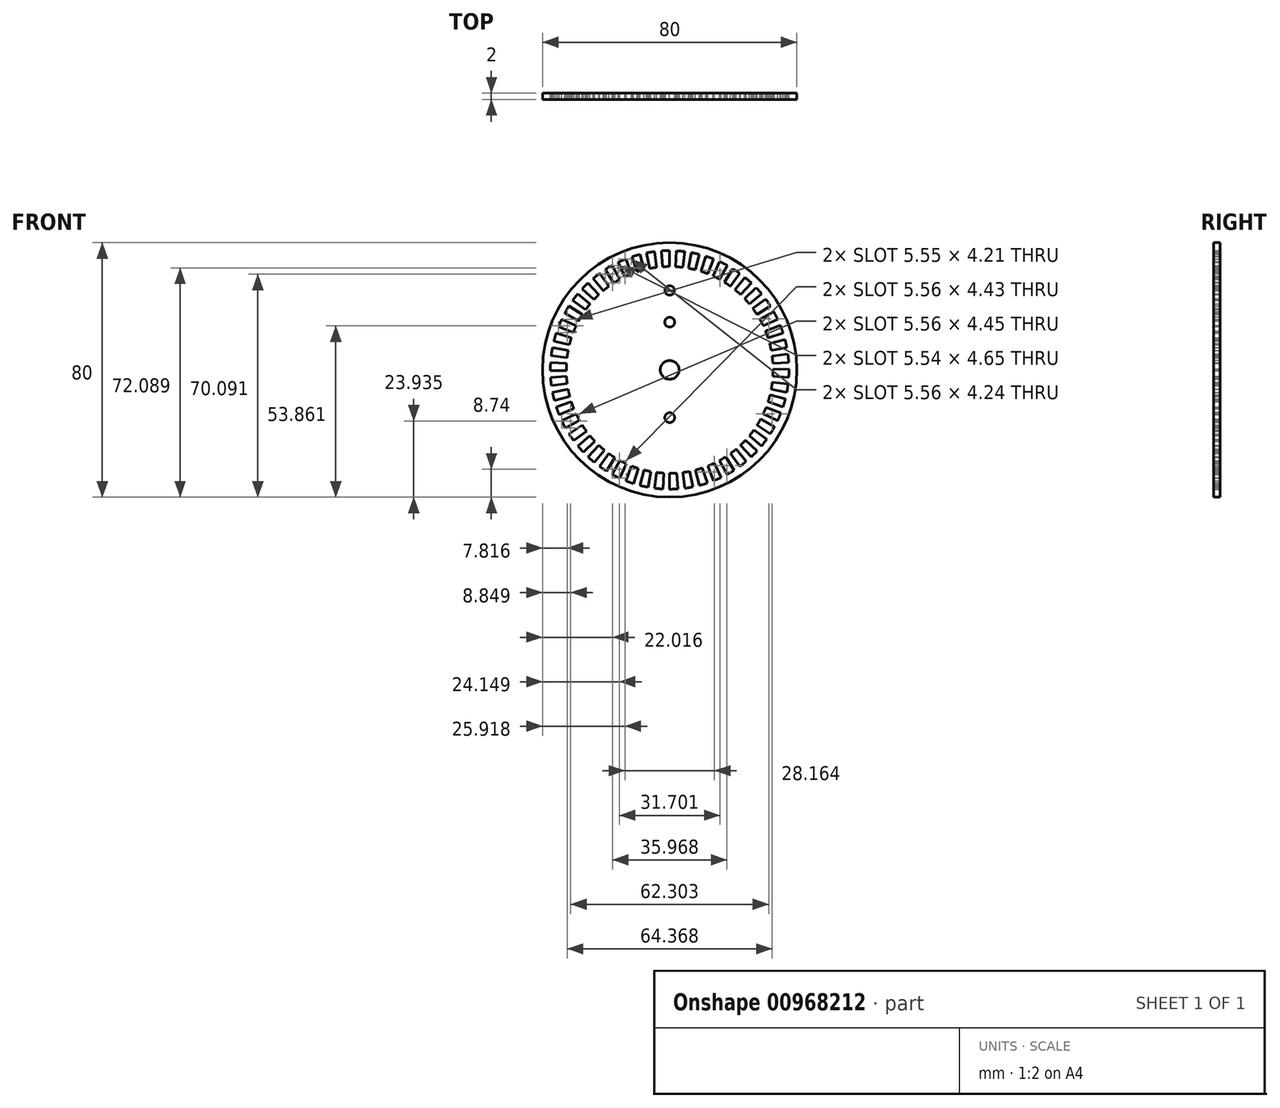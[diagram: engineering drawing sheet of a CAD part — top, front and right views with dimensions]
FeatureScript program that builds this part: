
annotation { "Feature Type Name" : "Feature", "Feature Type Description" : "" }
export const myFeature = defineFeature(function(context is Context, id is Id, definition is map)
    precondition{}
    {
        {
            var Q0;
            Q0=qCreatedBy(makeId("Front.planeOp"),FACE);
            var sketch = newSketch(context, id + "F0", { "sketchPlane" : qUnion([Q0])});
            skCircle(sketch, "E0", {"center": v(0, 0) * mm, "radius": 40 * mm});
            skSolve(sketch);
        }
        {
            var Q0;
            Q0=qSketchRegion(id+"F0",true);
            extrude(context, id + "F1", {"entities" : qUnion([Q0]), "endBound" : BoundingType.SYMMETRIC, "depth" : 2 * mm, "offsetDistance" : 25 * mm});
        }
        {
            var Q0;
            Q0=qCreatedBy(makeId("Front.planeOp"),FACE);
            var sketch = newSketch(context, id + "F2", { "sketchPlane" : qUnion([Q0])});
            skCircle(sketch, "E1", {"center": v(0, 0) * mm, "radius": 2.95 * mm});
            skCircle(sketch, "E2", {"center": v(0, 25) * mm, "radius": 1.5 * mm});
            skCircle(sketch, "E3", {"center": v(0, 15) * mm, "radius": 1.55 * mm});
            skCircle(sketch, "E4", {"center": v(0, -15) * mm, "radius": 1.55 * mm});
            skSolve(sketch);
        }
        {
            var Q0;
            Q0=qSketchRegion(id+"F2",true);
            extrude(context, id + "F3", {"entities" : qUnion([Q0]), "operationType" : NewBodyOperationType.REMOVE, "endBound" : BoundingType.SYMMETRIC, "oppositeDirection" : true, "depth" : 12 * mm, "offsetDistance" : 25 * mm});
        }
        {
            var Q0;
            Q0=qCreatedBy(makeId("Front.planeOp"),FACE);
            var sketch = newSketch(context, id + "F4", { "sketchPlane" : qUnion([Q0])});
            skLineSegment(sketch, "E5", {"start": v(0, 32.5) * mm, "end": v(0, 37.5) * mm});
            skArc(sketch, "E6", {"start": v(0, 37.5) * mm, "mid": v(-1.3, 37.48) * mm, "end": v(-2.61, 37.4) * mm});
            skArc(sketch, "E7", {"start": v(0, 32.5) * mm, "mid": v(-1.13, 32.48) * mm, "end": v(-2.26, 32.42) * mm});
            skLineSegment(sketch, "E8", {"start": v(-2.26, 32.42) * mm, "end": v(-2.61, 37.4) * mm});
            skLineSegment(sketch, "E9.1.0", {"start": v(-6.3, 31.88) * mm, "end": v(-7.28, 36.79) * mm});
            skLineSegment(sketch, "E9.1.1", {"start": v(-4.07, 32.24) * mm, "end": v(-4.7, 37.2) * mm});
            skArc(sketch, "E9.1.2", {"start": v(-4.7, 37.2) * mm, "mid": v(-6, 37.02) * mm, "end": v(-7.28, 36.79) * mm});
            skArc(sketch, "E9.1.3", {"start": v(-4.07, 32.24) * mm, "mid": v(-5.2, 32.08) * mm, "end": v(-6.3, 31.88) * mm});
            skLineSegment(sketch, "E9.2.0", {"start": v(-10.26, 30.84) * mm, "end": v(-11.83, 35.58) * mm});
            skLineSegment(sketch, "E9.2.1", {"start": v(-8.08, 31.48) * mm, "end": v(-9.33, 36.32) * mm});
            skArc(sketch, "E9.2.2", {"start": v(-9.33, 36.32) * mm, "mid": v(-10.59, 35.97) * mm, "end": v(-11.83, 35.58) * mm});
            skArc(sketch, "E9.2.3", {"start": v(-8.08, 31.48) * mm, "mid": v(-9.17, 31.18) * mm, "end": v(-10.26, 30.84) * mm});
            skLineSegment(sketch, "E9.3.0", {"start": v(-14.04, 29.31) * mm, "end": v(-16.2, 33.82) * mm});
            skLineSegment(sketch, "E9.3.1", {"start": v(-11.96, 30.22) * mm, "end": v(-13.8, 34.87) * mm});
            skArc(sketch, "E9.3.2", {"start": v(-13.8, 34.87) * mm, "mid": v(-15.01, 34.36) * mm, "end": v(-16.2, 33.82) * mm});
            skArc(sketch, "E9.3.3", {"start": v(-11.96, 30.22) * mm, "mid": v(-13, 29.78) * mm, "end": v(-14.04, 29.31) * mm});
            skLineSegment(sketch, "E9.4.0", {"start": v(-17.6, 27.32) * mm, "end": v(-20.31, 31.52) * mm});
            skLineSegment(sketch, "E9.4.1", {"start": v(-15.66, 28.48) * mm, "end": v(-18.07, 32.86) * mm});
            skArc(sketch, "E9.4.2", {"start": v(-18.07, 32.86) * mm, "mid": v(-19.2, 32.21) * mm, "end": v(-20.31, 31.52) * mm});
            skArc(sketch, "E9.4.3", {"start": v(-15.66, 28.48) * mm, "mid": v(-16.64, 27.92) * mm, "end": v(-17.6, 27.32) * mm});
            skLineSegment(sketch, "E9.5.0", {"start": v(-20.89, 24.9) * mm, "end": v(-24.1, 28.73) * mm});
            skLineSegment(sketch, "E9.5.1", {"start": v(-19.1, 26.3) * mm, "end": v(-22.04, 30.34) * mm});
            skArc(sketch, "E9.5.2", {"start": v(-22.04, 30.34) * mm, "mid": v(-23.09, 29.55) * mm, "end": v(-24.1, 28.73) * mm});
            skArc(sketch, "E9.5.3", {"start": v(-19.1, 26.3) * mm, "mid": v(-20, 25.61) * mm, "end": v(-20.89, 24.9) * mm});
            skLineSegment(sketch, "E9.6.0", {"start": v(-23.84, 22.08) * mm, "end": v(-27.51, 25.48) * mm});
            skLineSegment(sketch, "E9.6.1", {"start": v(-22.25, 23.7) * mm, "end": v(-25.67, 27.34) * mm});
            skArc(sketch, "E9.6.2", {"start": v(-25.67, 27.34) * mm, "mid": v(-26.6, 26.43) * mm, "end": v(-27.51, 25.48) * mm});
            skArc(sketch, "E9.6.3", {"start": v(-22.25, 23.7) * mm, "mid": v(-23.06, 22.9) * mm, "end": v(-23.84, 22.08) * mm});
            skLineSegment(sketch, "E9.7.0", {"start": v(-26.42, 18.92) * mm, "end": v(-30.49, 21.83) * mm});
            skLineSegment(sketch, "E9.7.1", {"start": v(-25.04, 20.72) * mm, "end": v(-28.9, 23.9) * mm});
            skArc(sketch, "E9.7.2", {"start": v(-28.9, 23.9) * mm, "mid": v(-29.7, 22.88) * mm, "end": v(-30.49, 21.83) * mm});
            skArc(sketch, "E9.7.3", {"start": v(-25.04, 20.72) * mm, "mid": v(-25.75, 19.83) * mm, "end": v(-26.42, 18.92) * mm});
            skLineSegment(sketch, "E9.8.0", {"start": v(-28.59, 15.46) * mm, "end": v(-32.98, 17.84) * mm});
            skLineSegment(sketch, "E9.8.1", {"start": v(-27.44, 17.41) * mm, "end": v(-31.66, 20.1) * mm});
            skArc(sketch, "E9.8.2", {"start": v(-31.66, 20.1) * mm, "mid": v(-32.34, 18.98) * mm, "end": v(-32.98, 17.84) * mm});
            skArc(sketch, "E9.8.3", {"start": v(-27.44, 17.41) * mm, "mid": v(-28.03, 16.45) * mm, "end": v(-28.59, 15.46) * mm});
            skLineSegment(sketch, "E9.9.0", {"start": v(-30.3, 11.76) * mm, "end": v(-34.96, 13.56) * mm});
            skLineSegment(sketch, "E9.9.1", {"start": v(-29.4, 13.84) * mm, "end": v(-33.93, 15.97) * mm});
            skArc(sketch, "E9.9.2", {"start": v(-33.93, 15.97) * mm, "mid": v(-34.47, 14.77) * mm, "end": v(-34.96, 13.56) * mm});
            skArc(sketch, "E9.9.3", {"start": v(-29.4, 13.84) * mm, "mid": v(-29.87, 12.8) * mm, "end": v(-30.3, 11.76) * mm});
            skLineSegment(sketch, "E9.10.0", {"start": v(-31.53, 7.87) * mm, "end": v(-36.39, 9.08) * mm});
            skLineSegment(sketch, "E9.10.1", {"start": v(-30.9, 10.04) * mm, "end": v(-35.66, 11.59) * mm});
            skArc(sketch, "E9.10.2", {"start": v(-35.66, 11.59) * mm, "mid": v(-36.05, 10.34) * mm, "end": v(-36.39, 9.08) * mm});
            skArc(sketch, "E9.10.3", {"start": v(-30.9, 10.04) * mm, "mid": v(-31.24, 8.96) * mm, "end": v(-31.53, 7.87) * mm});
            skLineSegment(sketch, "E9.11.0", {"start": v(-32.27, 3.85) * mm, "end": v(-37.24, 4.44) * mm});
            skLineSegment(sketch, "E9.11.1", {"start": v(-31.92, 6.09) * mm, "end": v(-36.84, 7.03) * mm});
            skArc(sketch, "E9.11.2", {"start": v(-36.84, 7.03) * mm, "mid": v(-37.06, 5.74) * mm, "end": v(-37.24, 4.44) * mm});
            skArc(sketch, "E9.11.3", {"start": v(-31.92, 6.09) * mm, "mid": v(-32.12, 4.97) * mm, "end": v(-32.27, 3.85) * mm});
            skLineSegment(sketch, "E9.12.0", {"start": v(-32.5, -0.22) * mm, "end": v(-37.5, -0.26) * mm});
            skLineSegment(sketch, "E9.12.1", {"start": v(-32.44, 2.04) * mm, "end": v(-37.43, 2.35) * mm});
            skArc(sketch, "E9.12.2", {"start": v(-37.43, 2.35) * mm, "mid": v(-37.49, 1.05) * mm, "end": v(-37.5, -0.26) * mm});
            skArc(sketch, "E9.12.3", {"start": v(-32.44, 2.04) * mm, "mid": v(-32.49, 0.9) * mm, "end": v(-32.5, -0.22) * mm});
            skLineSegment(sketch, "E9.13.0", {"start": v(-32.21, -4.3) * mm, "end": v(-37.17, -4.96) * mm});
            skLineSegment(sketch, "E9.13.1", {"start": v(-32.44, -2.04) * mm, "end": v(-37.43, -2.35) * mm});
            skArc(sketch, "E9.13.2", {"start": v(-37.43, -2.35) * mm, "mid": v(-37.32, -3.66) * mm, "end": v(-37.17, -4.96) * mm});
            skArc(sketch, "E9.13.3", {"start": v(-32.44, -2.04) * mm, "mid": v(-32.35, -3.17) * mm, "end": v(-32.21, -4.3) * mm});
            skLineSegment(sketch, "E9.14.0", {"start": v(-31.42, -8.3) * mm, "end": v(-36.26, -9.58) * mm});
            skLineSegment(sketch, "E9.14.1", {"start": v(-31.92, -6.09) * mm, "end": v(-36.84, -7.03) * mm});
            skArc(sketch, "E9.14.2", {"start": v(-36.84, -7.03) * mm, "mid": v(-36.57, -8.3) * mm, "end": v(-36.26, -9.58) * mm});
            skArc(sketch, "E9.14.3", {"start": v(-31.92, -6.09) * mm, "mid": v(-31.7, -7.2) * mm, "end": v(-31.42, -8.3) * mm});
            skLineSegment(sketch, "E9.15.0", {"start": v(-30.13, -12.17) * mm, "end": v(-34.77, -14.04) * mm});
            skLineSegment(sketch, "E9.15.1", {"start": v(-30.9, -10.04) * mm, "end": v(-35.66, -11.59) * mm});
            skArc(sketch, "E9.15.2", {"start": v(-35.66, -11.59) * mm, "mid": v(-35.24, -12.82) * mm, "end": v(-34.77, -14.04) * mm});
            skArc(sketch, "E9.15.3", {"start": v(-30.9, -10.04) * mm, "mid": v(-30.54, -11.11) * mm, "end": v(-30.13, -12.17) * mm});
            skLineSegment(sketch, "E9.16.0", {"start": v(-28.37, -15.85) * mm, "end": v(-32.74, -18.3) * mm});
            skLineSegment(sketch, "E9.16.1", {"start": v(-29.4, -13.84) * mm, "end": v(-33.93, -15.97) * mm});
            skArc(sketch, "E9.16.2", {"start": v(-33.93, -15.97) * mm, "mid": v(-33.35, -17.14) * mm, "end": v(-32.74, -18.3) * mm});
            skArc(sketch, "E9.16.3", {"start": v(-29.4, -13.84) * mm, "mid": v(-28.9, -14.85) * mm, "end": v(-28.37, -15.85) * mm});
            skLineSegment(sketch, "E9.17.0", {"start": v(-26.16, -19.28) * mm, "end": v(-30.19, -22.25) * mm});
            skLineSegment(sketch, "E9.17.1", {"start": v(-27.44, -17.41) * mm, "end": v(-31.66, -20.1) * mm});
            skArc(sketch, "E9.17.2", {"start": v(-31.66, -20.1) * mm, "mid": v(-30.94, -21.18) * mm, "end": v(-30.19, -22.25) * mm});
            skArc(sketch, "E9.17.3", {"start": v(-27.44, -17.41) * mm, "mid": v(-26.82, -18.36) * mm, "end": v(-26.16, -19.28) * mm});
            skLineSegment(sketch, "E9.18.0", {"start": v(-23.54, -22.41) * mm, "end": v(-27.16, -25.86) * mm});
            skLineSegment(sketch, "E9.18.1", {"start": v(-25.04, -20.72) * mm, "end": v(-28.9, -23.9) * mm});
            skArc(sketch, "E9.18.2", {"start": v(-28.9, -23.9) * mm, "mid": v(-28.04, -24.9) * mm, "end": v(-27.16, -25.86) * mm});
            skArc(sketch, "E9.18.3", {"start": v(-25.04, -20.72) * mm, "mid": v(-24.3, -21.58) * mm, "end": v(-23.54, -22.41) * mm});
            skLineSegment(sketch, "E9.19.0", {"start": v(-20.54, -25.18) * mm, "end": v(-23.7, -29.06) * mm});
            skLineSegment(sketch, "E9.19.1", {"start": v(-22.25, -23.7) * mm, "end": v(-25.67, -27.34) * mm});
            skArc(sketch, "E9.19.2", {"start": v(-25.67, -27.34) * mm, "mid": v(-24.7, -28.21) * mm, "end": v(-23.7, -29.06) * mm});
            skArc(sketch, "E9.19.3", {"start": v(-22.25, -23.7) * mm, "mid": v(-21.4, -24.45) * mm, "end": v(-20.54, -25.18) * mm});
            skLineSegment(sketch, "E9.20.0", {"start": v(-17.23, -27.56) * mm, "end": v(-19.88, -31.8) * mm});
            skLineSegment(sketch, "E9.20.1", {"start": v(-19.1, -26.3) * mm, "end": v(-22.04, -30.34) * mm});
            skArc(sketch, "E9.20.2", {"start": v(-22.04, -30.34) * mm, "mid": v(-20.97, -31.09) * mm, "end": v(-19.88, -31.8) * mm});
            skArc(sketch, "E9.20.3", {"start": v(-19.1, -26.3) * mm, "mid": v(-18.18, -26.94) * mm, "end": v(-17.23, -27.56) * mm});
            skLineSegment(sketch, "E9.21.0", {"start": v(-13.64, -29.5) * mm, "end": v(-15.73, -34.04) * mm});
            skLineSegment(sketch, "E9.21.1", {"start": v(-15.66, -28.48) * mm, "end": v(-18.07, -32.86) * mm});
            skArc(sketch, "E9.21.2", {"start": v(-18.07, -32.86) * mm, "mid": v(-16.9, -33.47) * mm, "end": v(-15.73, -34.04) * mm});
            skArc(sketch, "E9.21.3", {"start": v(-15.66, -28.48) * mm, "mid": v(-14.66, -29) * mm, "end": v(-13.64, -29.5) * mm});
            skLineSegment(sketch, "E9.22.0", {"start": v(-9.83, -30.98) * mm, "end": v(-11.34, -35.74) * mm});
            skLineSegment(sketch, "E9.22.1", {"start": v(-11.96, -30.22) * mm, "end": v(-13.8, -34.87) * mm});
            skArc(sketch, "E9.22.2", {"start": v(-13.8, -34.87) * mm, "mid": v(-12.58, -35.33) * mm, "end": v(-11.34, -35.74) * mm});
            skArc(sketch, "E9.22.3", {"start": v(-11.96, -30.22) * mm, "mid": v(-10.9, -30.62) * mm, "end": v(-9.83, -30.98) * mm});
            skLineSegment(sketch, "E9.23.0", {"start": v(-5.87, -31.97) * mm, "end": v(-6.77, -36.88) * mm});
            skLineSegment(sketch, "E9.23.1", {"start": v(-8.08, -31.48) * mm, "end": v(-9.33, -36.32) * mm});
            skArc(sketch, "E9.23.2", {"start": v(-9.33, -36.32) * mm, "mid": v(-8.05, -36.62) * mm, "end": v(-6.77, -36.88) * mm});
            skArc(sketch, "E9.23.3", {"start": v(-8.08, -31.48) * mm, "mid": v(-6.98, -31.74) * mm, "end": v(-5.87, -31.97) * mm});
            skLineSegment(sketch, "E9.24.0", {"start": v(-1.82, -32.45) * mm, "end": v(-2.1, -37.44) * mm});
            skLineSegment(sketch, "E9.24.1", {"start": v(-4.07, -32.24) * mm, "end": v(-4.7, -37.2) * mm});
            skArc(sketch, "E9.24.2", {"start": v(-4.7, -37.2) * mm, "mid": v(-3.4, -37.35) * mm, "end": v(-2.1, -37.44) * mm});
            skArc(sketch, "E9.24.3", {"start": v(-4.07, -32.24) * mm, "mid": v(-2.95, -32.37) * mm, "end": v(-1.82, -32.45) * mm});
            skLineSegment(sketch, "E9.25.0", {"start": v(2.26, -32.42) * mm, "end": v(2.61, -37.4) * mm});
            skLineSegment(sketch, "E9.25.1", {"start": v(0, -32.5) * mm, "end": v(0, -37.5) * mm});
            skArc(sketch, "E9.25.2", {"start": v(0, -37.5) * mm, "mid": v(1.3, -37.48) * mm, "end": v(2.61, -37.4) * mm});
            skArc(sketch, "E9.25.3", {"start": v(0, -32.5) * mm, "mid": v(1.13, -32.48) * mm, "end": v(2.26, -32.42) * mm});
            skLineSegment(sketch, "E9.26.0", {"start": v(6.3, -31.88) * mm, "end": v(7.28, -36.79) * mm});
            skLineSegment(sketch, "E9.26.1", {"start": v(4.07, -32.24) * mm, "end": v(4.7, -37.2) * mm});
            skArc(sketch, "E9.26.2", {"start": v(4.7, -37.2) * mm, "mid": v(6, -37.02) * mm, "end": v(7.28, -36.79) * mm});
            skArc(sketch, "E9.26.3", {"start": v(4.07, -32.24) * mm, "mid": v(5.2, -32.08) * mm, "end": v(6.3, -31.88) * mm});
            skLineSegment(sketch, "E9.27.0", {"start": v(10.26, -30.84) * mm, "end": v(11.83, -35.58) * mm});
            skLineSegment(sketch, "E9.27.1", {"start": v(8.08, -31.48) * mm, "end": v(9.33, -36.32) * mm});
            skArc(sketch, "E9.27.2", {"start": v(9.33, -36.32) * mm, "mid": v(10.59, -35.97) * mm, "end": v(11.83, -35.58) * mm});
            skArc(sketch, "E9.27.3", {"start": v(8.08, -31.48) * mm, "mid": v(9.17, -31.18) * mm, "end": v(10.26, -30.84) * mm});
            skLineSegment(sketch, "E9.28.0", {"start": v(14.04, -29.31) * mm, "end": v(16.2, -33.82) * mm});
            skLineSegment(sketch, "E9.28.1", {"start": v(11.96, -30.22) * mm, "end": v(13.8, -34.87) * mm});
            skArc(sketch, "E9.28.2", {"start": v(13.8, -34.87) * mm, "mid": v(15.01, -34.36) * mm, "end": v(16.2, -33.82) * mm});
            skArc(sketch, "E9.28.3", {"start": v(11.96, -30.22) * mm, "mid": v(13, -29.78) * mm, "end": v(14.04, -29.31) * mm});
            skLineSegment(sketch, "E9.29.0", {"start": v(17.6, -27.32) * mm, "end": v(20.31, -31.52) * mm});
            skLineSegment(sketch, "E9.29.1", {"start": v(15.66, -28.48) * mm, "end": v(18.07, -32.86) * mm});
            skArc(sketch, "E9.29.2", {"start": v(18.07, -32.86) * mm, "mid": v(19.2, -32.21) * mm, "end": v(20.31, -31.52) * mm});
            skArc(sketch, "E9.29.3", {"start": v(15.66, -28.48) * mm, "mid": v(16.64, -27.92) * mm, "end": v(17.6, -27.32) * mm});
            skLineSegment(sketch, "E9.30.0", {"start": v(20.89, -24.9) * mm, "end": v(24.1, -28.73) * mm});
            skLineSegment(sketch, "E9.30.1", {"start": v(19.1, -26.3) * mm, "end": v(22.04, -30.34) * mm});
            skArc(sketch, "E9.30.2", {"start": v(22.04, -30.34) * mm, "mid": v(23.09, -29.55) * mm, "end": v(24.1, -28.73) * mm});
            skArc(sketch, "E9.30.3", {"start": v(19.1, -26.3) * mm, "mid": v(20, -25.61) * mm, "end": v(20.89, -24.9) * mm});
            skLineSegment(sketch, "E9.31.0", {"start": v(23.84, -22.08) * mm, "end": v(27.51, -25.48) * mm});
            skLineSegment(sketch, "E9.31.1", {"start": v(22.25, -23.7) * mm, "end": v(25.67, -27.34) * mm});
            skArc(sketch, "E9.31.2", {"start": v(25.67, -27.34) * mm, "mid": v(26.6, -26.43) * mm, "end": v(27.51, -25.48) * mm});
            skArc(sketch, "E9.31.3", {"start": v(22.25, -23.7) * mm, "mid": v(23.06, -22.9) * mm, "end": v(23.84, -22.08) * mm});
            skLineSegment(sketch, "E9.32.0", {"start": v(26.42, -18.92) * mm, "end": v(30.49, -21.83) * mm});
            skLineSegment(sketch, "E9.32.1", {"start": v(25.04, -20.72) * mm, "end": v(28.9, -23.9) * mm});
            skArc(sketch, "E9.32.2", {"start": v(28.9, -23.9) * mm, "mid": v(29.7, -22.88) * mm, "end": v(30.49, -21.83) * mm});
            skArc(sketch, "E9.32.3", {"start": v(25.04, -20.72) * mm, "mid": v(25.75, -19.83) * mm, "end": v(26.42, -18.92) * mm});
            skLineSegment(sketch, "E9.33.0", {"start": v(28.59, -15.46) * mm, "end": v(32.98, -17.84) * mm});
            skLineSegment(sketch, "E9.33.1", {"start": v(27.44, -17.41) * mm, "end": v(31.66, -20.1) * mm});
            skArc(sketch, "E9.33.2", {"start": v(31.66, -20.1) * mm, "mid": v(32.34, -18.98) * mm, "end": v(32.98, -17.84) * mm});
            skArc(sketch, "E9.33.3", {"start": v(27.44, -17.41) * mm, "mid": v(28.03, -16.45) * mm, "end": v(28.59, -15.46) * mm});
            skLineSegment(sketch, "E9.34.0", {"start": v(30.3, -11.76) * mm, "end": v(34.96, -13.56) * mm});
            skLineSegment(sketch, "E9.34.1", {"start": v(29.4, -13.84) * mm, "end": v(33.93, -15.97) * mm});
            skArc(sketch, "E9.34.2", {"start": v(33.93, -15.97) * mm, "mid": v(34.47, -14.77) * mm, "end": v(34.96, -13.56) * mm});
            skArc(sketch, "E9.34.3", {"start": v(29.4, -13.84) * mm, "mid": v(29.87, -12.8) * mm, "end": v(30.3, -11.76) * mm});
            skLineSegment(sketch, "E9.35.0", {"start": v(31.53, -7.87) * mm, "end": v(36.39, -9.08) * mm});
            skLineSegment(sketch, "E9.35.1", {"start": v(30.9, -10.04) * mm, "end": v(35.66, -11.59) * mm});
            skArc(sketch, "E9.35.2", {"start": v(35.66, -11.59) * mm, "mid": v(36.05, -10.34) * mm, "end": v(36.39, -9.08) * mm});
            skArc(sketch, "E9.35.3", {"start": v(30.9, -10.04) * mm, "mid": v(31.24, -8.96) * mm, "end": v(31.53, -7.87) * mm});
            skLineSegment(sketch, "E9.36.0", {"start": v(32.27, -3.85) * mm, "end": v(37.24, -4.44) * mm});
            skLineSegment(sketch, "E9.36.1", {"start": v(31.92, -6.09) * mm, "end": v(36.84, -7.03) * mm});
            skArc(sketch, "E9.36.2", {"start": v(36.84, -7.03) * mm, "mid": v(37.06, -5.74) * mm, "end": v(37.24, -4.44) * mm});
            skArc(sketch, "E9.36.3", {"start": v(31.92, -6.09) * mm, "mid": v(32.12, -4.97) * mm, "end": v(32.27, -3.85) * mm});
            skLineSegment(sketch, "E9.37.0", {"start": v(32.5, 0.22) * mm, "end": v(37.5, 0.26) * mm});
            skLineSegment(sketch, "E9.37.1", {"start": v(32.44, -2.04) * mm, "end": v(37.43, -2.35) * mm});
            skArc(sketch, "E9.37.2", {"start": v(37.43, -2.35) * mm, "mid": v(37.49, -1.05) * mm, "end": v(37.5, 0.26) * mm});
            skArc(sketch, "E9.37.3", {"start": v(32.44, -2.04) * mm, "mid": v(32.49, -0.9) * mm, "end": v(32.5, 0.22) * mm});
            skLineSegment(sketch, "E9.38.0", {"start": v(32.21, 4.3) * mm, "end": v(37.17, 4.96) * mm});
            skLineSegment(sketch, "E9.38.1", {"start": v(32.44, 2.04) * mm, "end": v(37.43, 2.35) * mm});
            skArc(sketch, "E9.38.2", {"start": v(37.43, 2.35) * mm, "mid": v(37.32, 3.66) * mm, "end": v(37.17, 4.96) * mm});
            skArc(sketch, "E9.38.3", {"start": v(32.44, 2.04) * mm, "mid": v(32.35, 3.17) * mm, "end": v(32.21, 4.3) * mm});
            skLineSegment(sketch, "E9.39.0", {"start": v(31.42, 8.3) * mm, "end": v(36.26, 9.58) * mm});
            skLineSegment(sketch, "E9.39.1", {"start": v(31.92, 6.09) * mm, "end": v(36.84, 7.03) * mm});
            skArc(sketch, "E9.39.2", {"start": v(36.84, 7.03) * mm, "mid": v(36.57, 8.3) * mm, "end": v(36.26, 9.58) * mm});
            skArc(sketch, "E9.39.3", {"start": v(31.92, 6.09) * mm, "mid": v(31.7, 7.2) * mm, "end": v(31.42, 8.3) * mm});
            skLineSegment(sketch, "E9.40.0", {"start": v(30.13, 12.17) * mm, "end": v(34.77, 14.04) * mm});
            skLineSegment(sketch, "E9.40.1", {"start": v(30.9, 10.04) * mm, "end": v(35.66, 11.59) * mm});
            skArc(sketch, "E9.40.2", {"start": v(35.66, 11.59) * mm, "mid": v(35.24, 12.82) * mm, "end": v(34.77, 14.04) * mm});
            skArc(sketch, "E9.40.3", {"start": v(30.9, 10.04) * mm, "mid": v(30.54, 11.11) * mm, "end": v(30.13, 12.17) * mm});
            skLineSegment(sketch, "E9.41.0", {"start": v(28.37, 15.85) * mm, "end": v(32.74, 18.3) * mm});
            skLineSegment(sketch, "E9.41.1", {"start": v(29.4, 13.84) * mm, "end": v(33.93, 15.97) * mm});
            skArc(sketch, "E9.41.2", {"start": v(33.93, 15.97) * mm, "mid": v(33.35, 17.14) * mm, "end": v(32.74, 18.3) * mm});
            skArc(sketch, "E9.41.3", {"start": v(29.4, 13.84) * mm, "mid": v(28.9, 14.85) * mm, "end": v(28.37, 15.85) * mm});
            skLineSegment(sketch, "E9.42.0", {"start": v(26.16, 19.28) * mm, "end": v(30.19, 22.25) * mm});
            skLineSegment(sketch, "E9.42.1", {"start": v(27.44, 17.41) * mm, "end": v(31.66, 20.1) * mm});
            skArc(sketch, "E9.42.2", {"start": v(31.66, 20.1) * mm, "mid": v(30.94, 21.18) * mm, "end": v(30.19, 22.25) * mm});
            skArc(sketch, "E9.42.3", {"start": v(27.44, 17.41) * mm, "mid": v(26.82, 18.36) * mm, "end": v(26.16, 19.28) * mm});
            skLineSegment(sketch, "E9.43.0", {"start": v(23.54, 22.41) * mm, "end": v(27.16, 25.86) * mm});
            skLineSegment(sketch, "E9.43.1", {"start": v(25.04, 20.72) * mm, "end": v(28.9, 23.9) * mm});
            skArc(sketch, "E9.43.2", {"start": v(28.9, 23.9) * mm, "mid": v(28.04, 24.9) * mm, "end": v(27.16, 25.86) * mm});
            skArc(sketch, "E9.43.3", {"start": v(25.04, 20.72) * mm, "mid": v(24.3, 21.58) * mm, "end": v(23.54, 22.41) * mm});
            skLineSegment(sketch, "E9.44.0", {"start": v(20.54, 25.18) * mm, "end": v(23.7, 29.06) * mm});
            skLineSegment(sketch, "E9.44.1", {"start": v(22.25, 23.7) * mm, "end": v(25.67, 27.34) * mm});
            skArc(sketch, "E9.44.2", {"start": v(25.67, 27.34) * mm, "mid": v(24.7, 28.21) * mm, "end": v(23.7, 29.06) * mm});
            skArc(sketch, "E9.44.3", {"start": v(22.25, 23.7) * mm, "mid": v(21.4, 24.45) * mm, "end": v(20.54, 25.18) * mm});
            skLineSegment(sketch, "E9.45.0", {"start": v(17.23, 27.56) * mm, "end": v(19.88, 31.8) * mm});
            skLineSegment(sketch, "E9.45.1", {"start": v(19.1, 26.3) * mm, "end": v(22.04, 30.34) * mm});
            skArc(sketch, "E9.45.2", {"start": v(22.04, 30.34) * mm, "mid": v(20.97, 31.09) * mm, "end": v(19.88, 31.8) * mm});
            skArc(sketch, "E9.45.3", {"start": v(19.1, 26.3) * mm, "mid": v(18.18, 26.94) * mm, "end": v(17.23, 27.56) * mm});
            skLineSegment(sketch, "E9.46.0", {"start": v(13.64, 29.5) * mm, "end": v(15.73, 34.04) * mm});
            skLineSegment(sketch, "E9.46.1", {"start": v(15.66, 28.48) * mm, "end": v(18.07, 32.86) * mm});
            skArc(sketch, "E9.46.2", {"start": v(18.07, 32.86) * mm, "mid": v(16.9, 33.47) * mm, "end": v(15.73, 34.04) * mm});
            skArc(sketch, "E9.46.3", {"start": v(15.66, 28.48) * mm, "mid": v(14.66, 29) * mm, "end": v(13.64, 29.5) * mm});
            skLineSegment(sketch, "E9.47.0", {"start": v(9.83, 30.98) * mm, "end": v(11.34, 35.74) * mm});
            skLineSegment(sketch, "E9.47.1", {"start": v(11.96, 30.22) * mm, "end": v(13.8, 34.87) * mm});
            skArc(sketch, "E9.47.2", {"start": v(13.8, 34.87) * mm, "mid": v(12.58, 35.33) * mm, "end": v(11.34, 35.74) * mm});
            skArc(sketch, "E9.47.3", {"start": v(11.96, 30.22) * mm, "mid": v(10.9, 30.62) * mm, "end": v(9.83, 30.98) * mm});
            skLineSegment(sketch, "E9.48.0", {"start": v(5.87, 31.97) * mm, "end": v(6.77, 36.88) * mm});
            skLineSegment(sketch, "E9.48.1", {"start": v(8.08, 31.48) * mm, "end": v(9.33, 36.32) * mm});
            skArc(sketch, "E9.48.2", {"start": v(9.33, 36.32) * mm, "mid": v(8.05, 36.62) * mm, "end": v(6.77, 36.88) * mm});
            skArc(sketch, "E9.48.3", {"start": v(8.08, 31.48) * mm, "mid": v(6.98, 31.74) * mm, "end": v(5.87, 31.97) * mm});
            skLineSegment(sketch, "E9.49.0", {"start": v(1.82, 32.45) * mm, "end": v(2.1, 37.44) * mm});
            skLineSegment(sketch, "E9.49.1", {"start": v(4.07, 32.24) * mm, "end": v(4.7, 37.2) * mm});
            skArc(sketch, "E9.49.2", {"start": v(4.7, 37.2) * mm, "mid": v(3.4, 37.35) * mm, "end": v(2.1, 37.44) * mm});
            skArc(sketch, "E9.49.3", {"start": v(4.07, 32.24) * mm, "mid": v(2.95, 32.37) * mm, "end": v(1.82, 32.45) * mm});
            skSolve(sketch);
        }
        {
            var Q0;
            Q0=qSketchRegion(id+"F4",true);
            extrude(context, id + "F5", {"entities" : qUnion([Q0]), "operationType" : NewBodyOperationType.REMOVE, "endBound" : BoundingType.SYMMETRIC, "depth" : 25 * mm, "offsetDistance" : 25 * mm});
        }
    });
